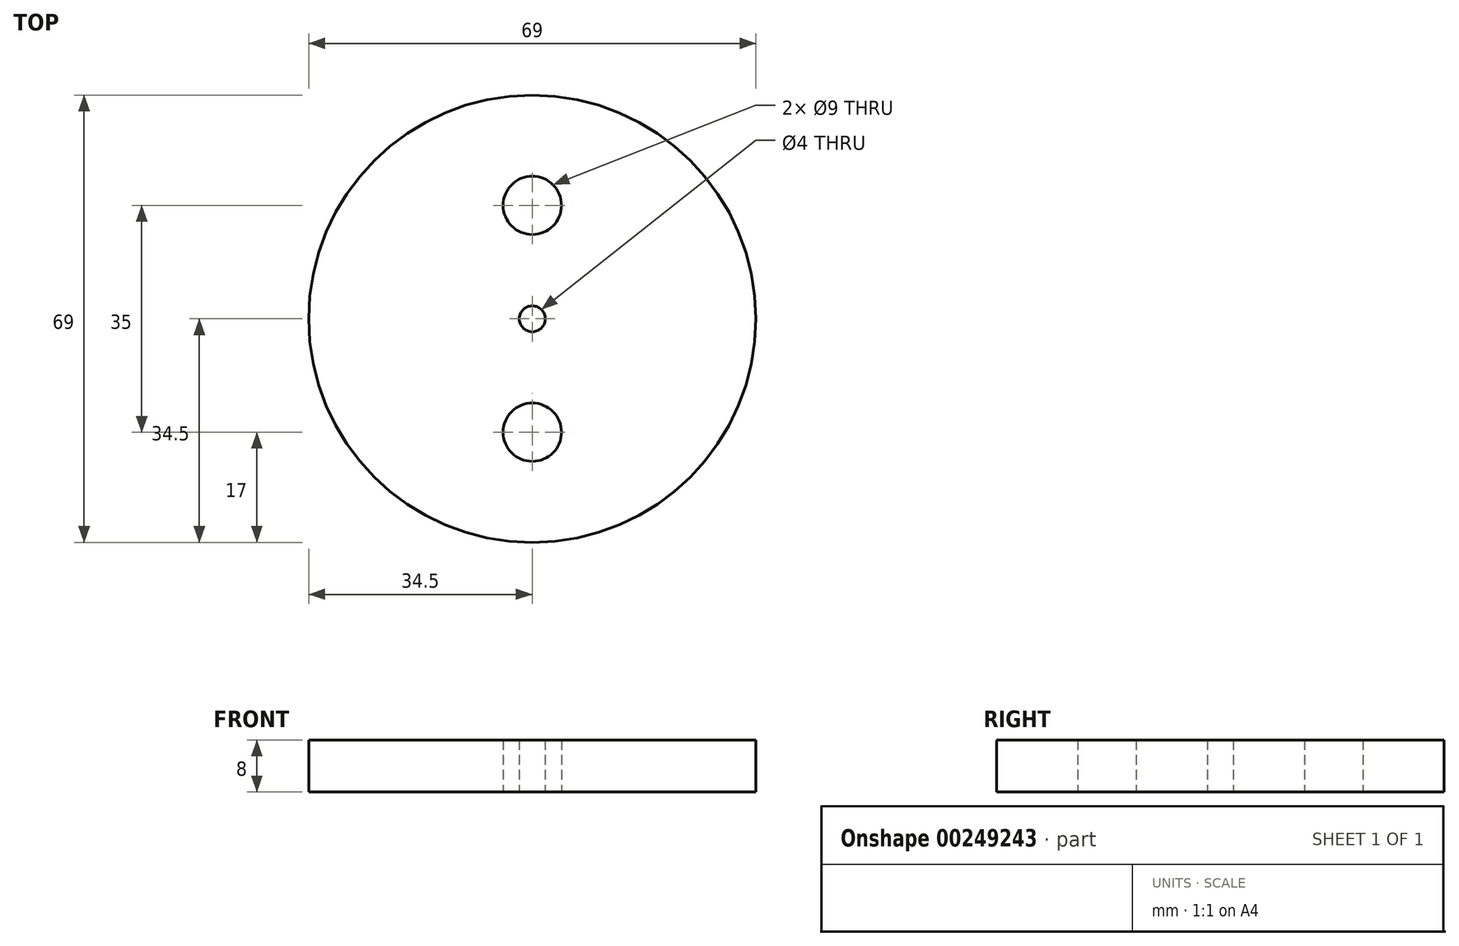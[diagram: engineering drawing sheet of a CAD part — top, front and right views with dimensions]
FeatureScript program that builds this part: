
annotation { "Feature Type Name" : "Feature", "Feature Type Description" : "" }
export const myFeature = defineFeature(function(context is Context, id is Id, definition is map)
    precondition{}
    {
        {
            var Q0;
            Q0=qCreatedBy(makeId("Top.planeOp"),FACE);
            var sketch = newSketch(context, id + "F0", { "sketchPlane" : qUnion([Q0])});
            skCircle(sketch, "E0", {"center": v(0, 0) * mm, "radius": 34.5 * mm});
            skCircle(sketch, "E1", {"center": v(0, 0) * mm, "radius": 2 * mm});
            skCircle(sketch, "E2", {"center": v(0, 0) * mm, "radius": 22 * mm});
            skCircle(sketch, "E3", {"center": v(0, 17.5) * mm, "radius": 4.5 * mm});
            skCircle(sketch, "E4", {"center": v(0, -17.5) * mm, "radius": 4.5 * mm});
            skSolve(sketch);
        }
        {
            var Q0;
            Q0=makeQuery(id+"F0.imprint","IMPRINT",FACE,{"disambiguationData":[TD([[makeQuery(id+"F0.imprint","IMPRINT",EDGE,{"derivedFrom":sQuery(id+"F0.wireOp",EDGE,"E1")}),-1.0]])]});
            var Q1;
            Q1=makeQuery(id+"F0.imprint","IMPRINT",FACE,{"disambiguationData":[TD([[makeQuery(id+"F0.imprint","IMPRINT",EDGE,{"derivedFrom":sQuery(id+"F0.wireOp",EDGE,"E0")}),1.0]])]});
            extrude(context, id + "F1", {"entities" : qUnion([Q0, Q1]), "depth" : 8 * mm});
        }
    });
